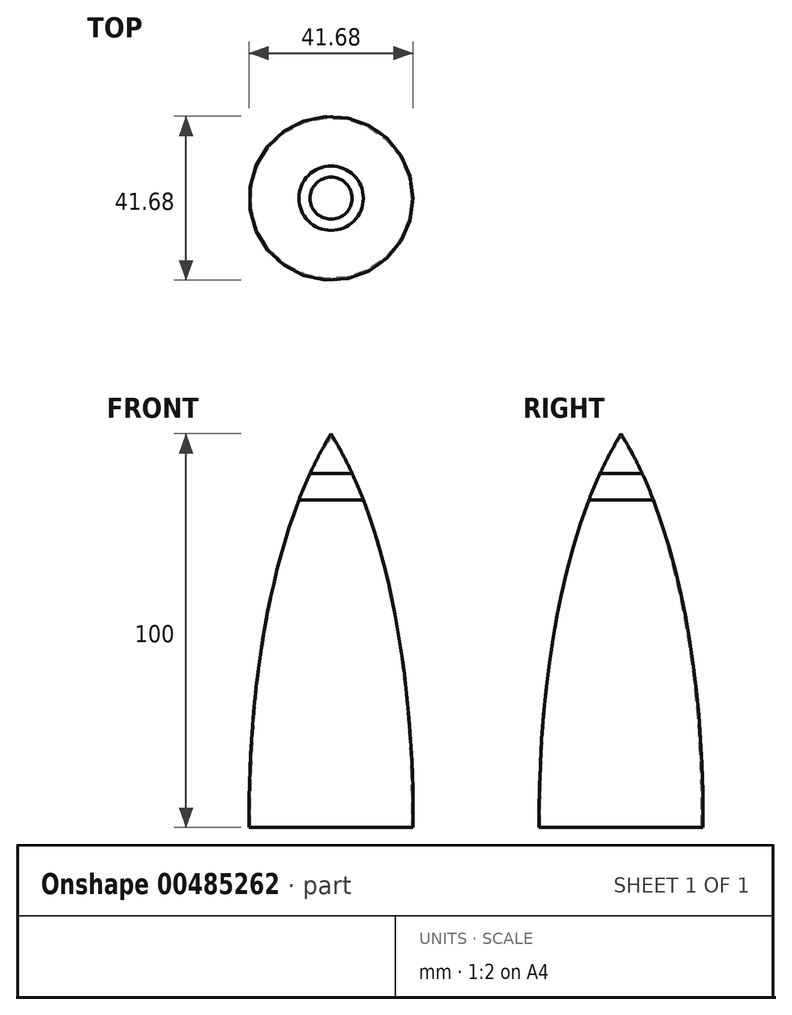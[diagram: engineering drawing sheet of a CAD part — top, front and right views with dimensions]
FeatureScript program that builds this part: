
annotation { "Feature Type Name" : "Feature", "Feature Type Description" : "" }
export const myFeature = defineFeature(function(context is Context, id is Id, definition is map)
    precondition{}
    {
        {
            var Q0;
            Q0=qCreatedBy(makeId("Front.planeOp"),FACE);
            var sketch = newSketch(context, id + "F0", { "sketchPlane" : qUnion([Q0])});
            skFitSpline(sketch, "E0", {"points": [v(0, 100) * mm, v(-20.83, 0) * mm, v(0, -65.85) * mm], "startDerivative": vector(-92, -150.37) * mm, "endDerivative": vector(115.04, -170.55) * mm});
            skFitSpline(sketch, "E1.0", {"points": [v(0.34, 99.8) * mm, v(-3.47, 93.56) * mm, v(-8.23, 83.01) * mm, v(-12.91, 67.57) * mm, v(-15.66, 55.55) * mm, v(-17.72, 43.34) * mm, v(-19.16, 31.2) * mm, v(-19.9, 21.33) * mm, v(-20.25, 13.72) * mm, v(-20.4, 8.18) * mm, v(-20.46, 2.85) * mm, v(-20.41, -2.25) * mm, v(-20.28, -7.1) * mm, v(-19.94, -13.3) * mm, v(-19.16, -20.64) * mm, v(-17.49, -29.1) * mm, v(-14.9, -37.5) * mm, v(-10.02, -49.05) * mm, v(-4.45, -58.54) * mm, v(0.33, -65.63) * mm]});
            skPoint(sketch, "E2.end.orphan", {"position": v(0, 0) * mm});
            skLineSegment(sketch, "E3", {"start": v(-20.83, 0) * mm, "end": v(-20.43, 0) * mm});
            skLineSegment(sketch, "E4", {"start": v(0, 100) * mm, "end": v(0, -20.65) * mm, "construction": true});
            skLineSegment(sketch, "E5", {"start": v(0, 100) * mm, "end": v(0, 99.23) * mm});
            skSolve(sketch);
        }
        {
            var Q0;
            Q0 = qSketchRegion(id + "F0", true);
            var Q1;
            Q1=sQuery(id+"F0.wireOp",EDGE,"E4");
            revolve(context, id + "F1", {"entities" : qUnion([Q0]), "axis" : qUnion([Q1]), "revolveType" : RevolveType.FULL});
        }
    });
